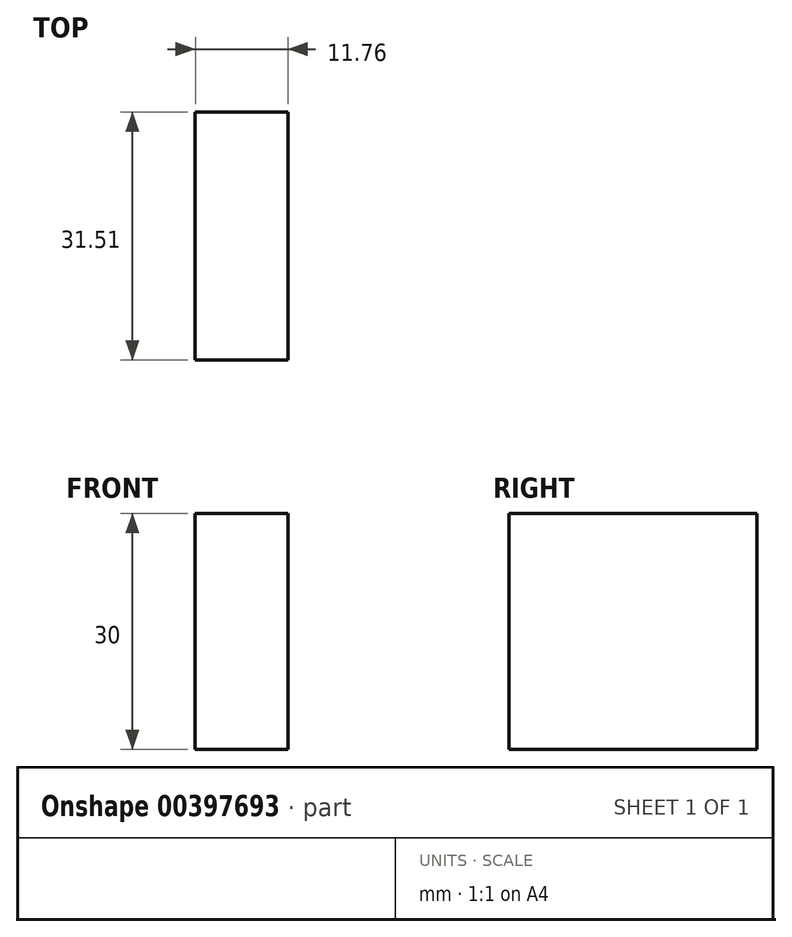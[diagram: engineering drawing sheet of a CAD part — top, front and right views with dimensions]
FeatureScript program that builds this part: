
annotation { "Feature Type Name" : "Feature", "Feature Type Description" : "" }
export const myFeature = defineFeature(function(context is Context, id is Id, definition is map)
    precondition{}
    {
        {
            var Q0;
            Q0=qCreatedBy(makeId("Top.planeOp"),FACE);
            var sketch = newSketch(context, id + "F0", { "sketchPlane" : qUnion([Q0])});
            skLineSegment(sketch, "E0.bottom", {"start": v(-33.4, 19.93) * mm, "end": v(-21.64, 19.93) * mm});
            skLineSegment(sketch, "E0.top", {"start": v(-33.4, -11.58) * mm, "end": v(-21.64, -11.58) * mm});
            skLineSegment(sketch, "E0.left", {"start": v(-33.4, 19.93) * mm, "end": v(-33.4, -11.58) * mm});
            skLineSegment(sketch, "E0.right", {"start": v(-21.64, 19.93) * mm, "end": v(-21.64, -11.58) * mm});
            skSolve(sketch);
        }
        {
            var Q0;
            Q0 = qSketchRegion(id + "F0", true);
            extrude(context, id + "F1", {"entities" : qUnion([Q0]), "depth" : 30 * mm});
        }
    });
